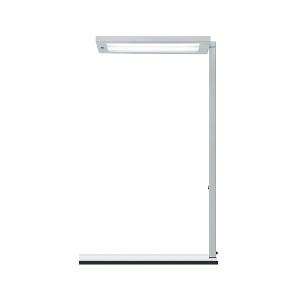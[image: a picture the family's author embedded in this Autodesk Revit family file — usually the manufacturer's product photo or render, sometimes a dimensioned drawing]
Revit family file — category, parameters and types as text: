
# Revit family: lavigo_core_-_dpt_9000_840_r_g1_ws_00812481_dfc5
name_source: partatom
category: Lighting Fixtures
units: mm (PartAtom-declared; Revit-internal decimal feet)

## family parameters
Cut with Voids When Loaded = No
Host = Face
Light Source = No
Part Type = Normal
Room Calculation Point = No
Round Connector Dimension = Use Diameter
Shared = No

## types (1)
- LAVIGO.core - DPT 9000/840/R/G1/WS (1 x LED, 8900 lm, 4000K)
    Apparent Load = 62 VA
    Approval mark = CE
    CIE Flux Codes = 59 88 97 35 100
    Color Rendering = 80-89
    Color Temperature = 4000K
    Control Gear = Electronic ballast
    Default Elevation = 1800 mm
    Description = DPT 9000/840/R/G1|Desk-mounted luminaire|light source: LED Cold white   |work equipment: Electronic ballast DALI|connected load: 220-240 V, 50/60 Hz|Power consumption: approx. 62 W|standby: approx. 0,30|power factor: approx. 0,959|luminous flux: 8900 lm|luminous efficacy: 143 lm/W|light distribution: Direct/indirect|direct ratio: approx. 35 %|color rendering index (CRI): >= 80|chromaticity tolerance:  3 SDCM|technology: Presence and daylight sensor control (PIR)|operation: Rocker switch|luminaire body|material: Steel/plastic|surface: Painted|colour: White|lamp cover: Polycarbonate (PC), Clear|tubular section|material: Steel tube|surface: Painted|Form: Tubular section upright|colour of tubular section: White|weight (net): approx. 8.3 kg|mains lead: 3.70 m Mains plug CEE 7/VII|Fastening: Socket, Table adaptor|decorative contrast side parts: Flint grey|glare control: Prism aperture|luminance(L65): <= 4400 cd/m|unified glare rating(4H 8H): <=  16|special features: Luminaire head detachable, Direct and indirect light switchable together, Flicker-free, Integrated light and presence sensor PIR, Motion sensor time-out of 15mins~|
    Frequency = 50 Hz, 60 Hz
    Height = 36 mm
    Lamp = 1 x LED
    Lamp Light Flux = 8900 lm
    Lamp count = 1
    Length = 675 mm
    Luminous efficacy = 144 lm/W
    Manufacturer = Waldmann
    ModVariant = No
    Model = 00812481
    Mounting Place = Floor
    Mounting Type = Freestanding
    Number of Poles = 1
    OnlyDefault = Yes
    Power Factor = 1
    Product Name = LAVIGO.core - DPT 9000/840/R/G1/WS
    Product group = Desk mounted luminaire with detector
    ProductGroupID = 2201
    Protection Class = Protection class I
    Protection Degree = IP 20
    RLX_Detail_Level = 1
    RLX_Emergency_Light_Flux = 0 lm
    RLX_Emergency_Type = 0
    RLX_Emergency_Type_DB = No
    RlxData = <blob elided: 31493 chars, md5=53f520e8>
    Socket = socket
    Standby Power = 0 W
    System Light Flux = 8900 lm
    System Power = 62 W
    Type Comments = Product without accessories
    Type Image = 121808000-00758540.jpg
    URL = http://relux.com
    VarID = ---
    Voltage = 230 V
    Voltage Range = 220-240 V
    Weight = 0.00 kg
    Width = 320 mm

## geometry (parser evidence)
native form markers: Blend x4, Sweep x14
no freeform markers — native parametric forms only
